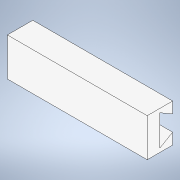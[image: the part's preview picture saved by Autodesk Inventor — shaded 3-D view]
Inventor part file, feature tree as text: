
AUTODESK INVENTOR PART (.ipt)
format: ipt  version: 2020.5 (Build 245400000, 400)  size: 101,376 bytes
history: native  units: mm
features: extrude x1, sketch x1
ambient origin geometry x8: Origin, YZ Plane, XZ Plane, XY Plane, X Axis, Y Axis, Z Axis, Center Point
bodies: Solid4 (feature_tree)
feature tree (2):
  extrude  "Extrusion3"  TaperAngle=60.0deg  [1 undecoded]
  sketch  "Sketch4"  dims[d31=60.0deg d32=60.0deg d33=10.0mm d34=12.0mm d35=110.0mm d36=0.0mm d43=10.0mm d44=30.0mm]
note: 1 required parameter value undecoded (feature->parameter linkage not recoverable at this tier; creation-order binding heuristic only, values carry confidence <= 0.55)
